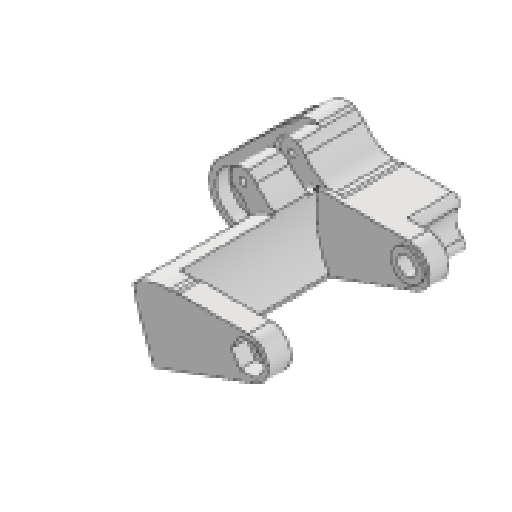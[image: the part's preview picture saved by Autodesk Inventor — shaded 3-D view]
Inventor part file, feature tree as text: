
AUTODESK INVENTOR PART (.ipt)
format: ipt  version: 2025 (Build 290162000, 162)  size: 585,728 bytes
history: native  units: mm
features: extrude x24, sketch x24, projected_geometry x21, fillet x10, other x9, reference x6, plane x1, thicken_offset x1
ambient origin geometry x8: Origin, YZ Plane, XZ Plane, XY Plane, X Axis, Y Axis, Z Axis, Center Point
bodies: Solid1 (feature_tree)
feature tree (96):
  extrude  "Extrusion1"  Depth=8.0mm
  extrude  "Extrusion2"  Depth=23.0mm
  extrude  "Extrusion3"  Depth=10.0mm TaperAngle=0.0deg
  extrude  "Extrusion4"  Depth=10.0mm TaperAngle=0.0deg
  extrude  "Extrusion5"  Depth=10.0mm
  extrude  "Extrusion6"  Depth=15.0mm
  extrude  "Extrusion7"  Depth=4.0mm TaperAngle=0.0deg
  extrude  "Extrusion8"  Depth=15.0mm TaperAngle=0.0deg
  fillet  "Fillet1"  Radius=15.0mm
  extrude  "Extrusion9"  Depth=15.0mm TaperAngle=0.0deg
  extrude  "Extrusion11"  Depth=15.0mm TaperAngle=0.0deg
  fillet  "Fillet2"  Radius=10.0mm
  extrude  "Extrusion12"  TaperAngle=0.0deg  [1 undecoded]
  extrude  "Extrusion13"  Depth=100.0mm
  extrude  "Extrusion14"  Depth=10.0mm TaperAngle=0.0deg
  extrude  "Extrusion15"  Depth=11.0mm
  extrude  "Extrusion16"  Depth=5.0mm
  fillet  "Fillet3"  Radius=5.0mm
  fillet  "Fillet4"  Radius=8.2mm
  fillet  "Fillet5"  Radius=5.0mm
  extrude  "Extrusion17"  Depth=1.0mm TaperAngle=0.0deg
  extrude  "Extrusion18"  Depth=1.0mm TaperAngle=0.0deg
  plane  "Work Plane1"
  extrude  "Extrusion19"  Depth=12.8mm
  fillet  "Fillet6"  Radius=1.0mm
  extrude  "Extrusion20"  Depth=7.0mm TaperAngle=0.0deg
  fillet  "Fillet7"  Radius=3.0mm
  extrude  "Extrusion21"  Depth=5.0mm
  extrude  "Extrusion22"  [1 undecoded]
  extrude  "Extrusion23"  [1 undecoded]
  extrude  "Extrusion24"  [1 undecoded]
  sketch  "Sketch25"
  thicken_offset  "Thicken1"
  extrude  "Extrusion25"  [1 undecoded]
  fillet  "Fillet9"  [1 undecoded]
  fillet  "Fillet10"  [1 undecoded]
  fillet  "Fillet11"  [1 undecoded]
  sketch  "Sketch1"  dims[d0=85.0mm d1=8.0mm]
  sketch  "Sketch2"  dims[d2=5.5mm d3=23.0mm]
  projected_geometry  "Projected Loop1"
  sketch  "Sketch3"  dims[d4=10.0mm d5=0.0mm d7=18.5mm d8=0.0mm]
  projected_geometry  "Projected Loop2"
  sketch  "Sketch4"  dims[d9=61.0mm d10=0.0mm d11=10.0mm d12=0.0mm]
  projected_geometry  "Projected Loop3"
  sketch  "Sketch5"  dims[d13=10.0mm d14=0.0mm d15=28.0mm]
  projected_geometry  "Projected Loop4"
  sketch  "Sketch6"  dims[d16=15.0mm d17=0.0mm d18=22.2mm]
  projected_geometry  "Projected Loop5"
  sketch  "Sketch7"  dims[d19=6.0mm d20=0.0mm d21=4.0mm d22=0.0mm]
  projected_geometry  "Projected Loop6"
  sketch  "Sketch8"  dims[d23=10.0mm d24=6.0mm d25=0.0mm d29=15.0mm d30=0.0mm]
  reference  "Reference1"
  projected_geometry  "Projected Loop7"
  reference  "Reference2"
  sketch  "Sketch9"  dims[d31=20.0mm d33=15.0mm d34=0.0mm]
  reference  "Reference3"
  sketch  "Sketch11"  dims[d35=3.1mm d36=15.0mm d37=0.0mm d38=10.0mm d39=0.0mm]
  projected_geometry  "Projected Loop8"
  sketch  "Sketch12"  dims[d40=16.0mm d41=0.0mm d42=0.0mm d43=0.0mm]
  projected_geometry  "Projected Loop9"
  sketch  "Sketch13"  dims[d44=20.0mm d45=100.0mm]
  projected_geometry  "Projected Loop10"
  projected_geometry  "Projected Loop11"
  reference  "Reference4"
  sketch  "Sketch14"  dims[d46=20.0mm d47=10.0mm d48=0.0mm]
  projected_geometry  "Projected Loop12"
  projected_geometry  "Projected Loop13"
  sketch  "Sketch15"  dims[d49=11.0mm d50=0.0mm d51=6.75mm]
  projected_geometry  "Projected Loop14"
  sketch  "Sketch16"  dims[d52=15.0mm d53=0.0mm d54=14.0mm d55=5.0mm d56=0.0mm d57=8.2mm d58=5.0mm]
  projected_geometry  "Projected Loop15"
  sketch  "Sketch17"  dims[d59=14.0mm d60=1.0mm d61=0.0mm]
  projected_geometry  "Projected Loop16"
  reference  "Reference5"
  reference  "Reference6"
  projected_geometry  "Projected Loop17"
  sketch  "Sketch18"  dims[d62=1.0mm d63=0.0mm d64=1.0mm d65=0.0mm]
  projected_geometry  "Projected Loop18"
  sketch  "Sketch19"  dims[d66=20.0mm d67=0.0mm d69=12.8mm d70=1.0mm]
  projected_geometry  "Projected Loop19"
  sketch  "Sketch20"  dims[d71=1.0mm d72=7.0mm d73=0.0mm d74=3.0mm]
  projected_geometry  "Projected Loop20"
  sketch  "Sketch21"  dims[d75=3.0mm d76=5.0mm]
  sketch  "Sketch22"  dims[d26=0.872665mm]
  sketch  "Sketch23"
  projected_geometry  "Projected Loop21"
  sketch  "Sketch24"
  other  "<userpath>\Desktop\puppycat\rearSwingarm.iam"
  other  "rearSwingarm.iam"
  other  "linkA:2"
  other  "b link:2"
  other  "6082rsBearing:15"
  other  "<userpath>\Desktop\puppycat\woodhouseMK1.iam"
  other  "woodhouseMK1.iam"
  other  "printedWheel:7"
  other  "6082rsBearing:73"
note: 8 required parameter values undecoded (feature->parameter linkage not recoverable at this tier; creation-order binding heuristic only, values carry confidence <= 0.55)
